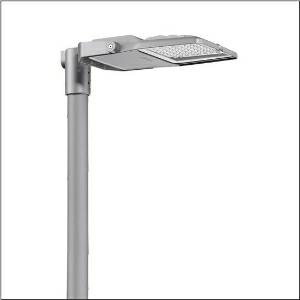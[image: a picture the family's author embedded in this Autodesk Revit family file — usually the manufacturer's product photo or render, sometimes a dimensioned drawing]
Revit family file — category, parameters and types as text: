
# Revit family: floodlight_fl_21_iq_mini___pl64_5xa7772b4e3a_29df
name_source: partatom
category: Lighting Fixtures
units: mm (PartAtom-declared; Revit-internal decimal feet)

## family parameters
Cut with Voids When Loaded = No
Host = Face
Light Source = No
Part Type = Normal
Room Calculation Point = No
Round Connector Dimension = Use Diameter
Shared = No

## types (1)
- --- (1 x LED, 6270 lm, 45.5 W, 4000K)
    Apparent Load = 46 VA
    CIE Flux Codes = 28 80 98 100 100
    Color Rendering = 70
    Color Temperature = 4000K
    Default Elevation = 1800 mm
    Description = Floodlight FL 21 iQ mini, floodlight, primary light control with lens, of PMMA, primary optical cover: protective disc, of toughened safety glass, transparent, light distribution: PL64, light emission: direct distribution, installation type: surface-mounted, LED, High Power LED, rated luminous flux: 6.270lm, luminous efficacy: 138lm/W, light colour: 740, colour temperature: 4000K, control gear: iQ Street-Remote/DALI, control: Auto-Match, Temp-Guard, Night-Set, Smart-Wire, Desk-Remote (wireless, voltage-free reading and setting of iQ features in the workshop via application-optimized NFC function/RFID function), optimised constant luminous flux control (CLO 2.0), Light-Fading, Lumen-Switch, with terminal, 6-pole, mains connection: 220..240V, AC, 50/60Hz, start of lifetime: 46W, end of service life: 48W, reduction: 22W, luminaire housing, of diecast aluminium, powder-coated, Siteco® metallic grey (DB 702S), corrosivity category C5 mid according to DIN EN ISO 12944, suitable for swimming pools, chlorine-resistant, sealing non-destructively replaceable, please order mast flange separately, mast bracket, of steel, galvanised, powder-coated, protection rating (complete): IP66, insulation class (complete): insulation class II (safety insulation), certification: CE, ENEC, VDE, protection symbol: D, impact resistance: IK08, permissible operating ambient temperature: -40..+40°C, permissible operating ambient temperature for outdoor applications: -40..+50°C, standard: DIN EN 12944, LABS conformity tested according to VDMA 24364:2018-05, packaging unit: 1 piece

Light Distribution: PL64
    Height = 70 mm
    Lamp = 1 x LED
    Lamp Light Flux = 6270 lm
    Lamp Power = 45.5 W
    Lamp count = 1
    Length = 485 mm
    Luminous efficacy = 138 lm/W
    Manufacturer = Siteco
    ModVariant = No
    Model = 5XA7772B4E3A
    Number of Poles = 1
    OnlyDefault = Yes
    Power Factor = 1
    Product Name = Floodlight FL 21 iQ mini | PL64
    Product group = floodlight | pylon annexe
    ProductGroupID = 6200
    Protection Class = Protection class II
    Protection Degree = IP 66
    RLX_Detail_Level = 1
    RLX_Emergency_Light_Flux = 0 lm
    RLX_Emergency_Type = 0
    RLX_Emergency_Type_DB = No
    RlxData = <blob elided: 101305 chars, md5=0968fe2c>
    Socket = socket
    Standby Power = 0 W
    System Light Flux = 6270 lm
    System Power = 46 W
    Type Comments = factory setting: luminous flux: 100 % | dim-lin: 254 | 463 mA
    Type Image = l_1007125.jpg
    URL = http://relux.com
    VarID = @adj_166758
    Voltage = 0 V
    Weight = 0.00 kg
    Width = 337 mm

## geometry (parser evidence)
native form markers: Blend x4, Sweep x13
no freeform markers — native parametric forms only
